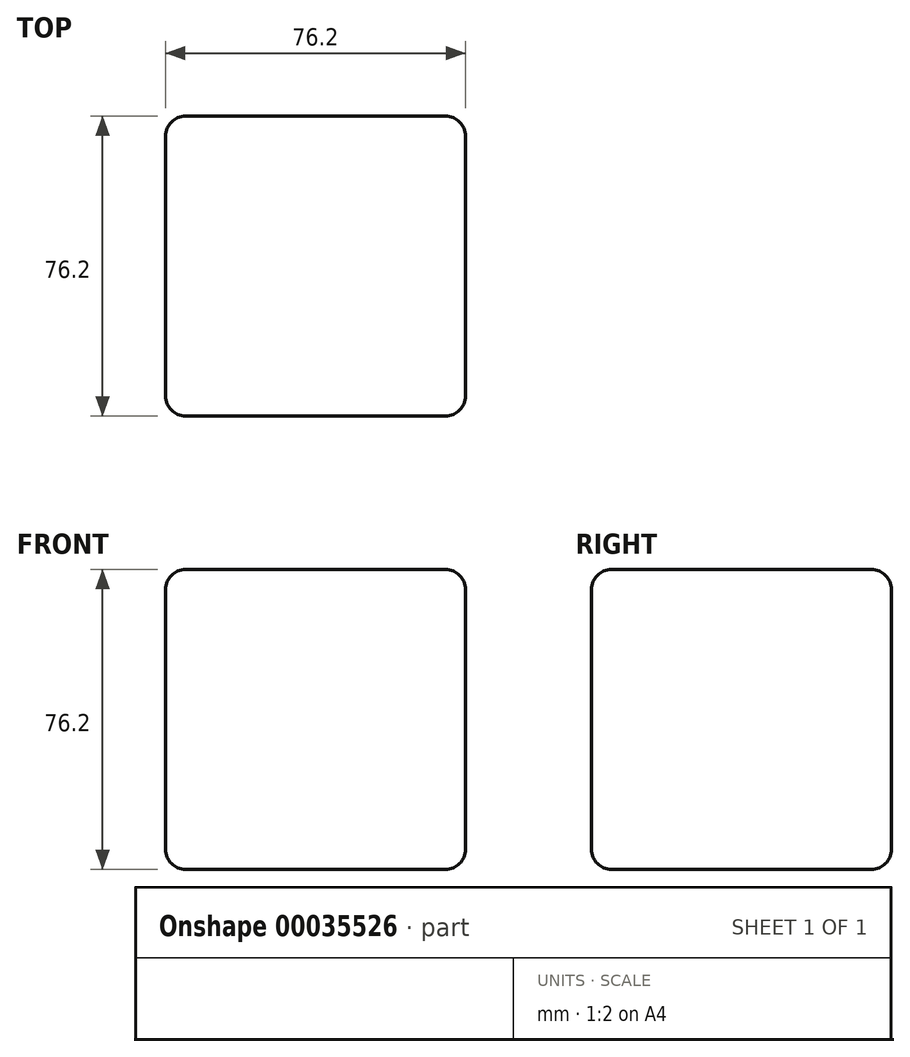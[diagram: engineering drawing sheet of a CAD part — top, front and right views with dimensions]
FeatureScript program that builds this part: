
annotation { "Feature Type Name" : "Feature", "Feature Type Description" : "" }
export const myFeature = defineFeature(function(context is Context, id is Id, definition is map)
    precondition{}
    {
        {
            var Q0;
            Q0=qCreatedBy(makeId("Top.planeOp"),FACE);
            var sketch = newSketch(context, id + "F0", { "sketchPlane" : qUnion([Q0])});
            skLineSegment(sketch, "E0.bottom", {"start": v(-61.77, 0) * mm, "end": v(14.43, 0) * mm});
            skLineSegment(sketch, "E0.top", {"start": v(-61.77, -76.2) * mm, "end": v(14.43, -76.2) * mm});
            skLineSegment(sketch, "E0.left", {"start": v(-61.77, 0) * mm, "end": v(-61.77, -76.2) * mm});
            skLineSegment(sketch, "E0.right", {"start": v(14.43, 0) * mm, "end": v(14.43, -76.2) * mm});
            skSolve(sketch);
        }
        {
            var Q0;
            Q0=makeQuery(id+"F0.imprint","IMPRINT",FACE,{"disambiguationData":[TD([[makeQuery(id+"F0.imprint","IMPRINT",EDGE,{"derivedFrom":sQuery(id+"F0.wireOp",EDGE,"E0.bottom")}),-1.0]])]});
            extrude(context, id + "F1", {"entities" : qUnion([Q0]), "depth" : 76.2 * mm});
        }
        {
            var Q0;
            Q0=makeQuery(id+"F1.opExtrude","SWEPT_FACE",FACE,{"disambiguationData":[OSD([sQuery(id+"F0.wireOp",EDGE,"E0.right")])]});
            var Q1;
            Q1=makeQuery(id+"F1.opExtrude","CAP_FACE",FACE,{"disambiguationData":[OSD([sQuery(id+"F0.wireOp",EDGE,"E0.bottom"),sQuery(id+"F0.wireOp",EDGE,"E0.top"),sQuery(id+"F0.wireOp",EDGE,"E0.left"),sQuery(id+"F0.wireOp",EDGE,"E0.right")])],"isStart":false});
            var Q2;
            Q2=makeQuery(id+"F1.opExtrude","SWEPT_FACE",FACE,{"disambiguationData":[OSD([sQuery(id+"F0.wireOp",EDGE,"E0.top")])]});
            var Q3;
            Q3=makeQuery(id+"F1.opExtrude","SWEPT_FACE",FACE,{"disambiguationData":[OSD([sQuery(id+"F0.wireOp",EDGE,"E0.bottom")])]});
            var Q4;
            Q4=makeQuery(id+"F1.opExtrude","SWEPT_FACE",FACE,{"disambiguationData":[OSD([sQuery(id+"F0.wireOp",EDGE,"E0.left")])]});
            var Q5;
            Q5=makeQuery(id+"F1.opExtrude","CAP_FACE",FACE,{"disambiguationData":[OSD([sQuery(id+"F0.wireOp",EDGE,"E0.bottom"),sQuery(id+"F0.wireOp",EDGE,"E0.top"),sQuery(id+"F0.wireOp",EDGE,"E0.left"),sQuery(id+"F0.wireOp",EDGE,"E0.right")])],"isStart":true});
            fillet(context, id + "F2", {"entities" : qUnion([Q0, Q1, Q2, Q3, Q4, Q5]), "radius" : 5.08 * mm, "tangentPropagation" : true, "allowEdgeOverflow" : false});
        }
        {
            var Q0;
            Q0=qCreatedBy(makeId("Front.planeOp"),FACE);
            cPlane(context, id + "F3", {"entities" : qUnion([Q0]), "cplaneType" : CPlaneType.OFFSET, "offset" : 152.4 * mm, "width" : 152.4 * mm, "height" : 152.4 * mm});
        }
    });
